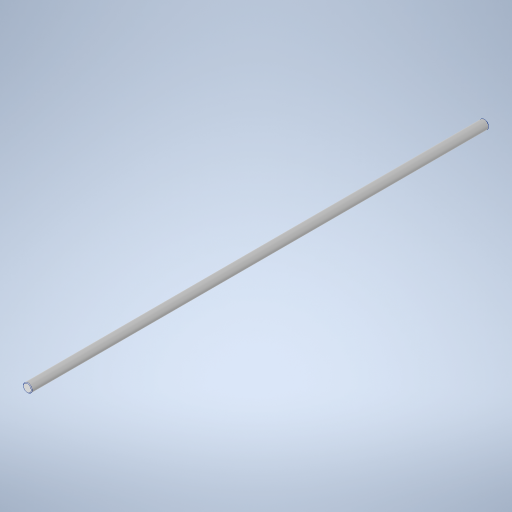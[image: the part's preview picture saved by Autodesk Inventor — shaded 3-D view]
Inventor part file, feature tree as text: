
AUTODESK INVENTOR PART (.ipt)
format: ipt  version: 2024 (Build 280153000, 153)  size: 246,272 bytes
history: native  units: mm
features: extrude x1, chamfer x1, sketch x1
ambient origin geometry x8: Origin, YZ Plane, XZ Plane, XY Plane, X Axis, Y Axis, Z Axis, Center Point
bodies: Solid1 (feature_tree)
feature tree (3):
  extrude  "Extrusion1"  Depth=415.0mm TaperAngle=0.0deg
  chamfer  "Chamfer1"  Distance=0.5mm Angle=45.0deg
  sketch  "Sketch1"  dims[d0=8.0mm d1=415.0mm d2=0.0mm d3=0.5mm d4=2.0mm d5=45.0deg]
